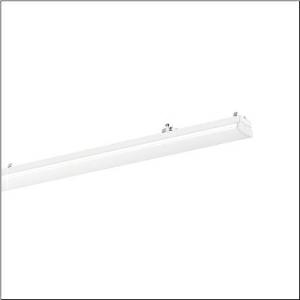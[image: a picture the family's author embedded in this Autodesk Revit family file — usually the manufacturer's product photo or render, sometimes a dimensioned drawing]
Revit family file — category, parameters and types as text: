
# Revit family: licross_21_recessed_opal_ho_52te1ddv4l2m
name_source: partatom
category: Lighting Fixtures
units: mm (PartAtom-declared; Revit-internal decimal feet)

## family parameters
Cut with Voids When Loaded = No
Host = Face
Light Source = No
Part Type = Normal
Room Calculation Point = No
Round Connector Dimension = Use Diameter
Shared = No

## types (1)
- --- (1 x LED, 22050 lm, 125.6 W, 4000K)
    Apparent Load = 126 VA
    CIE Flux Codes = 44 73 91 87 100
    Color Rendering = 80
    Color Temperature = 4000K
    Default Elevation = 1800 mm
    Description = Licross 21 recessed opal HO, luminaire insert, of sheet steel, galvanised, coil coated, white, length: 2.250mm, width: 66mm, height: 67mm, LED rated luminous flux: 22.050lm, light colour: 840, SDCM (Standard Deviation of Colour Matching)MacAdam ≤ 3 SDCM (initial), control gear: DALI 2, with plug, 5-pole, with phase selection, mains connection: 220..240V, AC, 50/60Hz, rated input power: 126W, internal wiring halogen-free, primary optical cover: cover, of PMMA, light emission: direct with ceiling illumination distribution, primary light characteristic: symmetric, protection rating (complete): IP54, insulation class (complete): insulation class I (protective earthing), certification: CE, ENEC, VDE, UKCA, protection symbol: D if used in an environment with non-conductive dust loads with corresponding accessories, impact resistance: IK06, permissible ambient temperature for indoor applications: -40..+30°C, corresponds to IFS (International Featured Standards) requirements for safety and quality in the food industry, reducing of maximum allowable ambient temperature of 5°C with ceiling mounting, LABS conformity tested according to VDMA 24364:2018-05, The light source and the operating device comply with the requirements of the Ecodesign Regulation (EU) 2019/2020 and are replaceable in accordance with this regulation, packaging unit: 1 piece
    Height = 83 mm
    Lamp = 1 x LED
    Lamp Light Flux = 22050 lm
    Lamp Power = 125.6 W
    Lamp count = 1
    Length = 2250 mm
    Luminous efficacy = 176 lm/W
    Manufacturer = Siteco
    ModVariant = No
    Model = 52TE1DDV4L2M
    Mounting Place = Ceiling
    Mounting Type = Pendant
    Number of Poles = 1
    OnlyDefault = Yes
    Power Factor = 1
    Product Name = Licross 21 recessed opal HO
    Product group = luminaire insert | ceiling pendant
    ProductGroupID = 901
    Protection Class = Protection class I
    Protection Degree = IP 54
    RLX_Detail_Level = 1
    RLX_Emergency_Light_Flux = 0 lm
    RLX_Emergency_Type = 0
    RLX_Emergency_Type_DB = No
    RlxData = <blob elided: 27081 chars, md5=e420ea5c>
    Socket = socket
    Standby Power = 0 W
    System Light Flux = 22050 lm
    System Power = 126 W
    Type Comments = factory setting: luminous flux: 100 % | dim-lin: 254 | 489 mA
    Type Image = l_1313666.jpg
    URL = http://relux.com
    VarID = @adj_072439
    Voltage = 0 V
    Weight = 0.00 kg
    Width = 76 mm

## geometry (parser evidence)
native form markers: Blend x4, Sweep x14
no freeform markers — native parametric forms only
